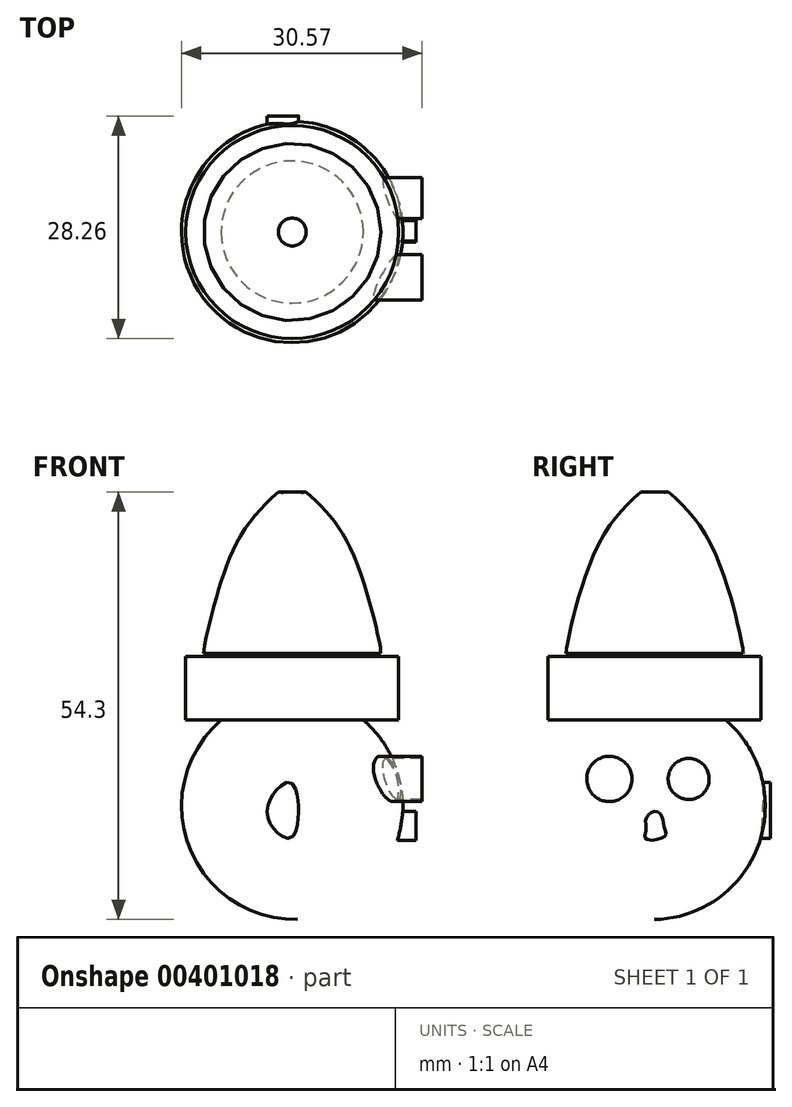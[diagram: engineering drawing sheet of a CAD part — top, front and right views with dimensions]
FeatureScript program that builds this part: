
annotation { "Feature Type Name" : "Feature", "Feature Type Description" : "" }
export const myFeature = defineFeature(function(context is Context, id is Id, definition is map)
    precondition{}
    {
        {
            var Q0;
            Q0=qCreatedBy(makeId("Right.planeOp"),FACE);
            var sketch = newSketch(context, id + "F0", { "sketchPlane" : qUnion([Q0])});
            skArc(sketch, "E0", {"start": v(0, -28.78) * mm, "mid": v(14.06, -14.4) * mm, "end": v(0, 0) * mm});
            skLineSegment(sketch, "E1", {"start": v(0, 76.27) * mm, "end": v(0, -51.8) * mm});
            skSolve(sketch);
        }
        {
            var Q0;
            Q0 = qSketchRegion(id + "F0", true);
            var Q1;
            Q1=sQuery(id+"F0.wireOp",EDGE,"E1");
            revolve(context, id + "F1", {"entities" : qUnion([Q0]), "axis" : qUnion([Q1]), "revolveType" : RevolveType.FULL});
        }
        {
            var Q0;
            Q0=qCreatedBy(makeId("Right.planeOp"),FACE);
            var sketch = newSketch(context, id + "F2", { "sketchPlane" : qUnion([Q0])});
            skLineSegment(sketch, "E2", {"start": v(0, 4.6) * mm, "end": v(13.53, 4.6) * mm});
            skLineSegment(sketch, "E3", {"start": v(13.53, 4.6) * mm, "end": v(13.53, -3.45) * mm});
            skLineSegment(sketch, "E4", {"start": v(13.53, -3.45) * mm, "end": v(0, -3.45) * mm});
            skLineSegment(sketch, "E5", {"start": v(0, -3.45) * mm, "end": v(0, 4.6) * mm});
            skSolve(sketch);
        }
        {
            var Q0;
            Q0=makeQuery(id+"F2.imprint","IMPRINT",FACE,{"disambiguationData":[TD([[makeQuery(id+"F2.imprint","IMPRINT",EDGE,{"derivedFrom":sQuery(id+"F2.wireOp",EDGE,"E2")}),-1.0]])]});
            var Q1;
            Q1=sQuery(id+"F2.wireOp",EDGE,"E5");
            revolve(context, id + "F3", {"operationType" : NewBodyOperationType.ADD, "entities" : qUnion([Q0]), "axis" : qUnion([Q1]), "revolveType" : RevolveType.FULL});
        }
        {
            var Q0;
            Q0=qCreatedBy(makeId("Right.planeOp"),FACE);
            var sketch = newSketch(context, id + "F4", { "sketchPlane" : qUnion([Q0])});
            skFitSpline(sketch, "E6", {"points": [v(0, 27.05) * mm, v(4.32, 23.02) * mm, v(8.35, 16.12) * mm, v(11.22, 5.47) * mm, v(11.22, 4.9) * mm], "startDerivative": vector(17.28, -14.72) * mm, "endDerivative": vector(-0.72, -4.52) * mm});
            skLineSegment(sketch, "E7", {"start": v(0, 27.05) * mm, "end": v(0, 4.9) * mm});
            skLineSegment(sketch, "E8", {"start": v(0, 4.9) * mm, "end": v(11.24, 5.02) * mm});
            skSolve(sketch);
        }
        {
            var Q0;
            {var subQ0=sQuery(id+"F4.wireOp",EDGE,"E7");Q0=makeQuery(id+"F4.imprint","IMPRINT",FACE,{"disambiguationData":[TD([[makeQuery(id+"F4.imprint","IMPRINT",EDGE,{"derivedFrom":subQ0}),1.0]])]});}
            var Q1;
            Q1=sQuery(id+"F4.wireOp",EDGE,"E7");
            revolve(context, id + "F5", {"entities" : qUnion([Q0]), "axis" : qUnion([Q1]), "revolveType" : RevolveType.FULL});
        }
        {
            var Q0;
            Q0=qCreatedBy(makeId("Right.planeOp"),FACE);
            var sketch = newSketch(context, id + "F6", { "sketchPlane" : qUnion([Q0])});
            skArc(sketch, "E9", {"start": v(0, 25.33) * mm, "mid": v(3.51, 28.2) * mm, "end": v(0, 31.08) * mm});
            skLineSegment(sketch, "E10", {"start": v(0, 31.08) * mm, "end": v(0, 25.33) * mm});
            skSolve(sketch);
        }
        {
            var Q0;
            Q0 = qSketchRegion(id + "F6", true);
            var Q1;
            Q1=sQuery(id+"F6.wireOp",EDGE,"E10");
            revolve(context, id + "F7", {"operationType" : NewBodyOperationType.ADD, "entities" : qUnion([Q0]), "axis" : qUnion([Q1]), "revolveType" : RevolveType.FULL});
        }
        {
            var Q0;
            Q0=qCreatedBy(makeId("Right.planeOp"),FACE);
            var sketch = newSketch(context, id + "F8", { "sketchPlane" : qUnion([Q0])});
            skCircle(sketch, "E11", {"center": v(-5.76, -10.94) * mm, "radius": 2.88 * mm});
            skSolve(sketch);
        }
        {
            var Q0;
            Q0=makeQuery(id+"F8.imprint","IMPRINT",FACE,{"disambiguationData":[TD([[makeQuery(id+"F8.imprint","IMPRINT",EDGE,{"derivedFrom":sQuery(id+"F8.wireOp",EDGE,"E11")}),1.0]])]});
            extrude(context, id + "F9", {"entities" : qUnion([Q0]), "operationType" : NewBodyOperationType.ADD, "depth" : 16.5 * mm});
        }
        {
            var Q0;
            Q0=qCreatedBy(makeId("Right.planeOp"),FACE);
            var sketch = newSketch(context, id + "F10", { "sketchPlane" : qUnion([Q0])});
            skCircle(sketch, "E12", {"center": v(4.32, -10.94) * mm, "radius": 2.6 * mm});
            skSolve(sketch);
        }
        {
            var Q0;
            Q0 = qSketchRegion(id + "F10", true);
            extrude(context, id + "F11", {"entities" : qUnion([Q0]), "operationType" : NewBodyOperationType.ADD, "depth" : 16.5 * mm});
        }
        {
            var Q0;
            Q0=qCreatedBy(makeId("Front.planeOp"),FACE);
            var sketch = newSketch(context, id + "F12", { "sketchPlane" : qUnion([Q0])});
            skFitSpline(sketch, "E13", {"points": [v(0, -12.09) * mm, v(-2.6, -12.95) * mm, v(-3.17, -14.68) * mm, v(-2.88, -16.98) * mm, v(0, -17.56) * mm, v(0, -12.09) * mm]});
            skSolve(sketch);
        }
        {
            var Q0;
            Q0 = qSketchRegion(id + "F12", true);
            extrude(context, id + "F13", {"entities" : qUnion([Q0]), "operationType" : NewBodyOperationType.ADD, "depth" : 15 * mm});
        }
        {
            var Q0;
            Q0=qCreatedBy(makeId("Front.planeOp"),FACE);
            var sketch = newSketch(context, id + "F14", { "sketchPlane" : qUnion([Q0])});
            skFitSpline(sketch, "E14", {"points": [v(0, -11.52) * mm, v(-2.5, -13.01) * mm, v(-3.2, -15.2) * mm, v(-2.44, -17.13) * mm, v(0, -18.31) * mm, v(0, -11.52) * mm]});
            skSolve(sketch);
        }
        {
            var Q0;
            Q0 = qSketchRegion(id + "F14", true);
            extrude(context, id + "F15", {"entities" : qUnion([Q0]), "operationType" : NewBodyOperationType.ADD, "oppositeDirection" : true, "depth" : 14.73 * mm});
        }
        {
            var Q0;
            Q0=qCreatedBy(makeId("Right.planeOp"),FACE);
            var sketch = newSketch(context, id + "F16", { "sketchPlane" : qUnion([Q0])});
            skFitSpline(sketch, "E15", {"points": [v(0, -15.04) * mm, v(0.95, -15.77) * mm, v(1.2, -16.98) * mm, v(1.32, -18.19) * mm, v(-1.1, -18.55) * mm, v(-1.1, -17.34) * mm, v(-1.1, -16.01) * mm, v(0, -15.04) * mm]});
            skSolve(sketch);
        }
        {
            var Q0;
            Q0 = qSketchRegion(id + "F16", true);
            extrude(context, id + "F17", {"entities" : qUnion([Q0]), "operationType" : NewBodyOperationType.ADD, "depth" : 15.75 * mm});
        }
        {
            var Q0;
            Q0=qCreatedBy(makeId("Right.planeOp"),FACE);
            var sketch = newSketch(context, id + "F18", { "sketchPlane" : qUnion([Q0])});
            skArc(sketch, "E16", {"start": v(-4.6, -21.59) * mm, "mid": v(-0.14, -25.32) * mm, "end": v(4.32, -21.59) * mm});
            skLineSegment(sketch, "E17", {"start": v(-4.6, -21.59) * mm, "end": v(4.32, -21.59) * mm});
            skSolve(sketch);
        }
        {
            var Q0;
            Q0 = qSketchRegion(id + "F18", true);
            extrude(context, id + "F19", {"entities" : qUnion([Q0]), "operationType" : NewBodyOperationType.ADD, "depth" : 13.2 * mm});
        }
    });
